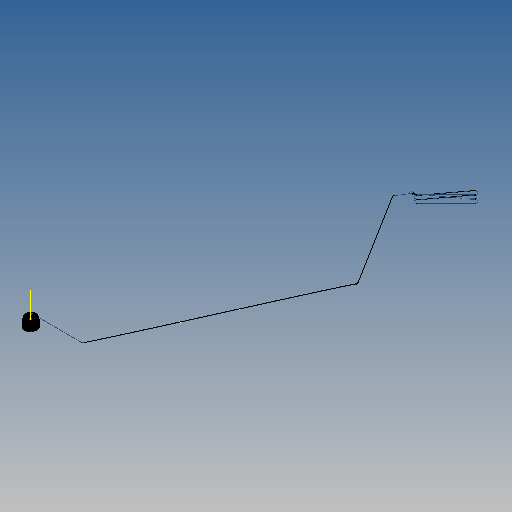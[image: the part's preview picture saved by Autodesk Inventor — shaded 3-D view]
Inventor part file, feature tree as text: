
AUTODESK INVENTOR PART (.ipt)
format: ipt  version: 2025.1 (Build 291241000, 241)  size: 624,128 bytes
history: native  units: mm
features: other x17, sketch x14, plane x11, sweep x5, loft x5, projected_geometry x1, extrude x1
ambient origin geometry x8: Origin, YZ Plane, XZ Plane, XY Plane, X Axis, Y Axis, Z Axis, Center Point
bodies: Volumenkörper1 (feature_tree)
feature tree (54):
  sketch  "Skizze1"  dims[d0=25.0mm d1=16.459mm]
  plane  "Arbeitsebene1"
  sketch  "Skizze2"  dims[d2=93.749mm d3=8.0mm]
  plane  "Arbeitsebene2"
  sweep  "Sweeping1"
  plane  "Arbeitsebene3"
  sketch  "Skizze4"  dims[d6=254.756mm d7=284.058mm]
  plane  "Arbeitsebene4"
  sweep  "Sweeping2"
  loft  "Erhebung1"
  plane  "Arbeitsebene5"
  sketch  "Skizze6"  dims[d10=614.727mm d11=614.797mm]
  plane  "Arbeitsebene6"
  sweep  "Sweeping3"
  loft  "Erhebung2"
  sketch  "Skizze9"  dims[d16=0.5mm d17=0.5mm]
  other  "Arbeitsachse1"
  plane  "Arbeitsebene8"
  sweep  "Sweeping5"
  plane  "Arbeitsebene9"
  sweep  "Sweeping6"
  loft  "Erhebung3"
  other  "Spirale1"
  plane  "Arbeitsebene10"
  other  "Spirale2"
  loft  "Erhebung4"
  plane  "Arbeitsebene11"
  other  "Spirale3"
  loft  "Erhebung5"
  sketch  "Skizze3"  dims[d4=171.709mm d5=194.197mm]
  sketch  "Skizze5"  dims[d8=395.434mm d9=592.03mm]
  sketch  "Skizze7"  dims[d12=676.109mm d13=7.2mm]
  other  "Kanten3"
  other  "Kanten4"
  sketch  "Skizze8"  dims[d14=182.883mm d15=0.5mm]
  other  "Flä1"
  other  "Arbeitsachse2"
  plane  "Arbeitsebene7"
  sketch  "Skizze10"  dims[d18=0.5mm d19=0.5mm]
  other  "Kanten5"
  other  "Kanten6"
  sketch  "Skizze11"  dims[d20=20.0mm d21=8.0mm]
  other  "Kanten7"
  other  "Kanten8"
  sketch  "Skizze12"  dims[d22=8.0mm]
  sketch  "Skizze13"  dims[d23=0.5mm]
  other  "Kanten9"
  other  "Kanten10"
  sketch  "Skizze14"  dims[d24=2.9mm d25=0.0mm d26=0.5mm d27=3.0mm d28=0.0mm d29=1.534024mm d30=1.434024mm d31=1.0mm d32=0.0mm d33=0.0mm d34=12.0mm d35=0.5mm d36=1.0mm d37=0.0mm d38=0.0mm d39=2.5mm d40=90.0deg d43=4.0mm d44=0.5mm d45=1.0mm d46=0.0mm d47=0.0mm d48=2.5mm d49=90.0deg d50=2.5mm d51=90.0deg d52=30.0mm d53=0.0mm d54=90.0deg d57=0.0mm d58=0.0mm d59=10.0mm d60=2.5mm d61=90.0deg d62=1.0mm d63=0.0mm d64=0.0mm d65=5.0mm d66=90.0deg d67=5.0mm d68=90.0deg d69=1.001mm d70=13.5mm d71=10.0mm d72=0.0mm d73=90.0deg d74=90.0deg d75=0.0mm d76=0.0mm d77=90.0deg d78=1.0mm d79=11.5mm d80=1.001mm d81=19.0mm d82=10.0mm d83=0.0mm d84=90.0deg d85=90.0deg d86=0.0mm d87=0.0mm d88=10.0mm d89=90.0deg d90=12.5mm d91=90.0deg d92=90.0deg d93=10.5mm d94=1.0mm d95=1.001mm d96=19.0mm d97=10.0mm d98=0.0mm d99=90.0deg d100=90.0deg d101=0.0mm d102=0.0mm d103=10.0mm d104=90.0deg d105=12.5mm d106=90.0deg]
  projected_geometry  "Projizierte Kontur1"
  other  "Kanten11"
  other  "Kanten12"
  extrude  "Extrusionsfläche1"  Depth=8.0mm
  other  "Schnittkanten projizieren1"
